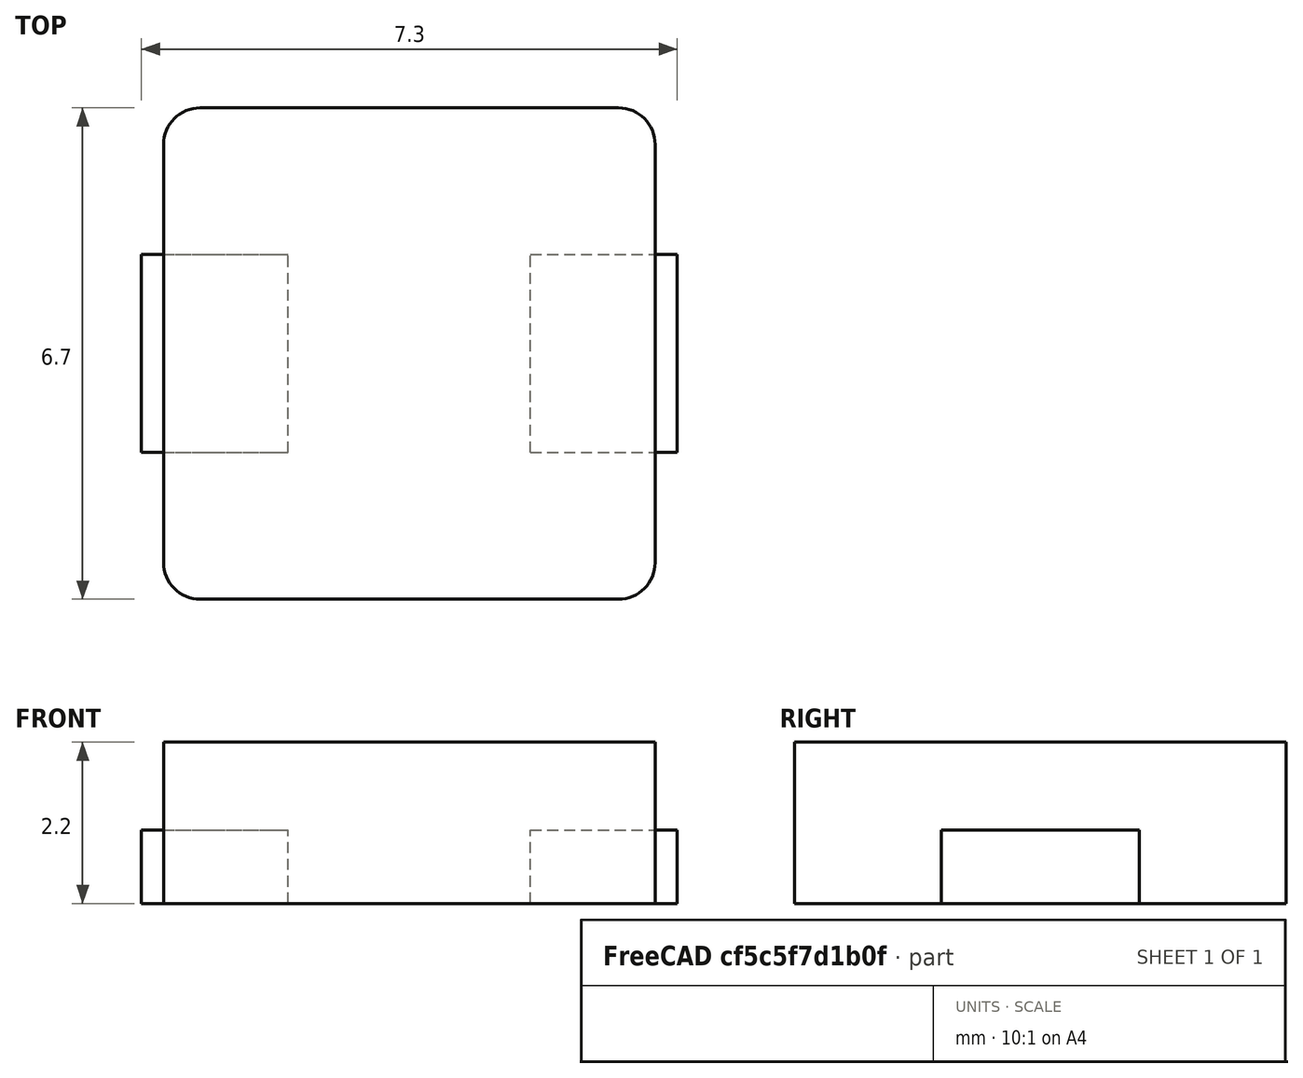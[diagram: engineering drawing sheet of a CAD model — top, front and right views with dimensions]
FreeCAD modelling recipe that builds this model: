
FCSTD DOCUMENT  (FreeCAD 0.18R4 (GitTag))
Label: inductor_hpi0624
License: All rights reserved
LicenseURL: http://en.wikipedia.org/wiki/All_rights_reserved
objects: Part::Feature×4, Part::Box×3, Part::Cut×2, Part::Fillet×1, App::Part×1
note: 10 computed .brp shape members not serialized (recipe doc carries the construction recipe); baked Part::Feature solids carry a one-line shape summary decoded from their .brp

FEATURE [Part::Box] Box  label="body"
  AttacherType = Attacher::AttachEngine3D
  Height = 2.2
  Length = 6.7
  Placement = pos=(-3.35,-3.35,0) rot=(0,0,1;0rad)
  Width = 6.7
FEATURE [Part::Box] Box001  label="pad1"
  AttacherType = Attacher::AttachEngine3D
  Height = 1
  Length = 2
  Placement = pos=(1.65,-1.35,0) rot=(0,0,1;0rad)
  Width = 2.7
FEATURE [Part::Box] Box002  label="pad2"
  AttacherType = Attacher::AttachEngine3D
  Height = 1
  Length = 2
  Placement = pos=(-3.65,-1.35,0) rot=(0,0,1;0rad)
  Width = 2.7
FEATURE [Part::Fillet] Fillet
  Base = -> Box
  Edges = 4 edges r=0.5: [Edge1,Edge3,Edge5,Edge7]
FEATURE [Part::Cut] Cut
  Base = -> Fillet
  Tool = -> Box002
FEATURE [Part::Cut] Cut001
  Base = -> Cut
  Tool = -> Box001
FEATURE [App::Part] Part  label="inductor_hpi0624"
  Group = -> [Box,Box001,Box002,Fillet,Cut,Cut001]
  Origin = -> Origin
FEATURE [Part::Feature] Box001_cp  label="pad1_cp"
  Placement = pos=(1.65,-1.35,0) rot=(0,0,1;0rad)
  shape: bbox 2 x 2.7 x 1 mm, 6 faces (baked)
FEATURE [Part::Feature] Box002_cp  label="pad2_cp"
  Placement = pos=(-3.65,-1.35,0) rot=(0,0,1;0rad)
  shape: bbox 2 x 2.7 x 1 mm, 6 faces (baked)
FEATURE [Part::Feature] Cut001_cp
  shape: bbox 6.7 x 6.7 x 2.2 mm, 18 faces (baked)
FEATURE [Part::Feature] Shape  label="inductor_hpi0624_cp"
  shape: bbox 7.3 x 6.7 x 2.2 mm, 30 faces, 3 solids (baked)
